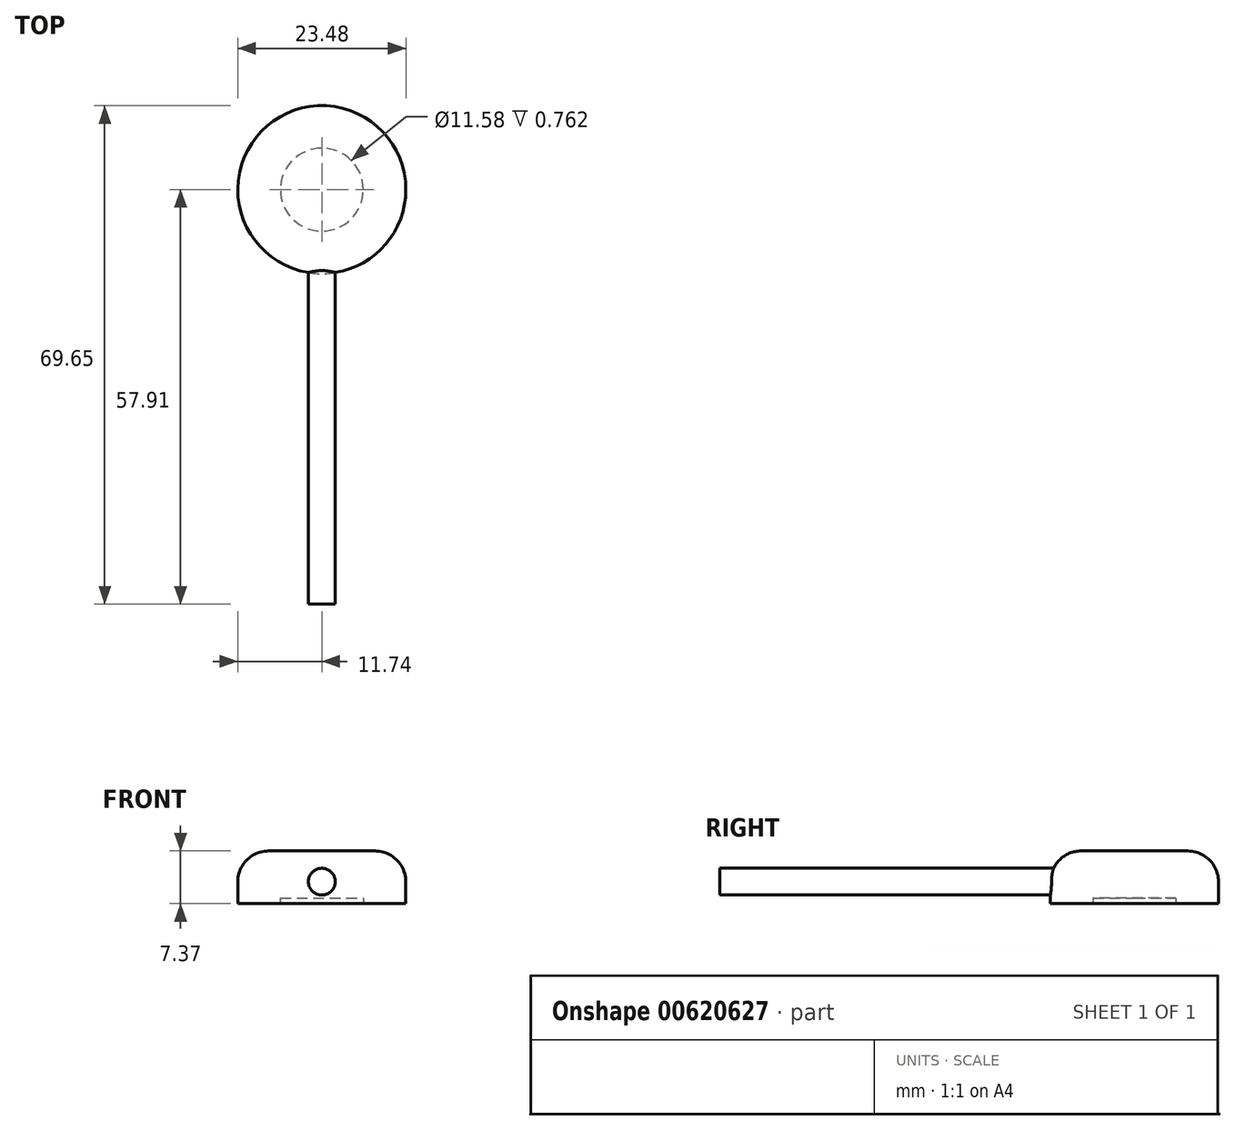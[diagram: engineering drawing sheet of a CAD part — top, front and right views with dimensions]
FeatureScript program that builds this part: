
annotation { "Feature Type Name" : "Feature", "Feature Type Description" : "" }
export const myFeature = defineFeature(function(context is Context, id is Id, definition is map)
    precondition{}
    {
        {
            var Q0;
            Q0=qCreatedBy(makeId("Top.planeOp"),FACE);
            var sketch = newSketch(context, id + "F0", { "sketchPlane" : qUnion([Q0])});
            skCircle(sketch, "E0", {"center": v(0, 0) * mm, "radius": 11.74 * mm});
            skSolve(sketch);
        }
        {
            var Q0;
            Q0=makeQuery(id+"F0.imprint","IMPRINT",FACE,{"disambiguationData":[TD([[makeQuery(id+"F0.imprint","IMPRINT",EDGE,{"derivedFrom":sQuery(id+"F0.wireOp",EDGE,"E0")}),1.0]])]});
            extrude(context, id + "F1", {"entities" : qUnion([Q0]), "depth" : 7.37 * mm, "offsetDistance" : 25.4 * mm});
        }
        {
            var Q0;
            Q0=makeQuery(id+"F1.opExtrude","CAP_EDGE",EDGE,{"disambiguationData":[OSD([sQuery(id+"F0.wireOp",EDGE,"E0")])],"isStart":false});
            fillet(context, id + "F2", {"entities" : qUnion([Q0]), "radius" : 4.3 * mm, "tangentPropagation" : true, "allowEdgeOverflow" : false});
        }
        {
            var Q0;
            Q0=makeQuery(id+"F1.opExtrude","CAP_FACE",FACE,{"disambiguationData":[OSD([sQuery(id+"F0.wireOp",EDGE,"E0")])],"isStart":true});
            var sketch = newSketch(context, id + "F3", { "sketchPlane" : qUnion([Q0])});
            skCircle(sketch, "E1", {"center": v(0, 0) * mm, "radius": 5.8 * mm});
            skSolve(sketch);
        }
        {
            var Q0;
            Q0=makeQuery(id+"F3.imprint","IMPRINT",FACE,{"disambiguationData":[TD([[makeQuery(id+"F3.imprint","IMPRINT",EDGE,{"derivedFrom":sQuery(id+"F3.wireOp",EDGE,"E1")}),1.0]])]});
            extrude(context, id + "F4", {"entities" : qUnion([Q0]), "operationType" : NewBodyOperationType.REMOVE, "oppositeDirection" : true, "depth" : 0.76 * mm, "offsetDistance" : 25.4 * mm});
        }
        {
            var Q0;
            Q0=qCreatedBy(makeId("Front.planeOp"),FACE);
            var sketch = newSketch(context, id + "F5", { "sketchPlane" : qUnion([Q0])});
            skCircle(sketch, "E2", {"center": v(0, 3.07) * mm, "radius": 1.88 * mm});
            skSolve(sketch);
        }
        {
            var Q0;
            Q0 = qSketchRegion(id + "F5", true);
            extrude(context, id + "F6", {"entities" : qUnion([Q0]), "operationType" : NewBodyOperationType.ADD, "depth" : 57.9 * mm, "offsetDistance" : 25.4 * mm});
        }
    });
